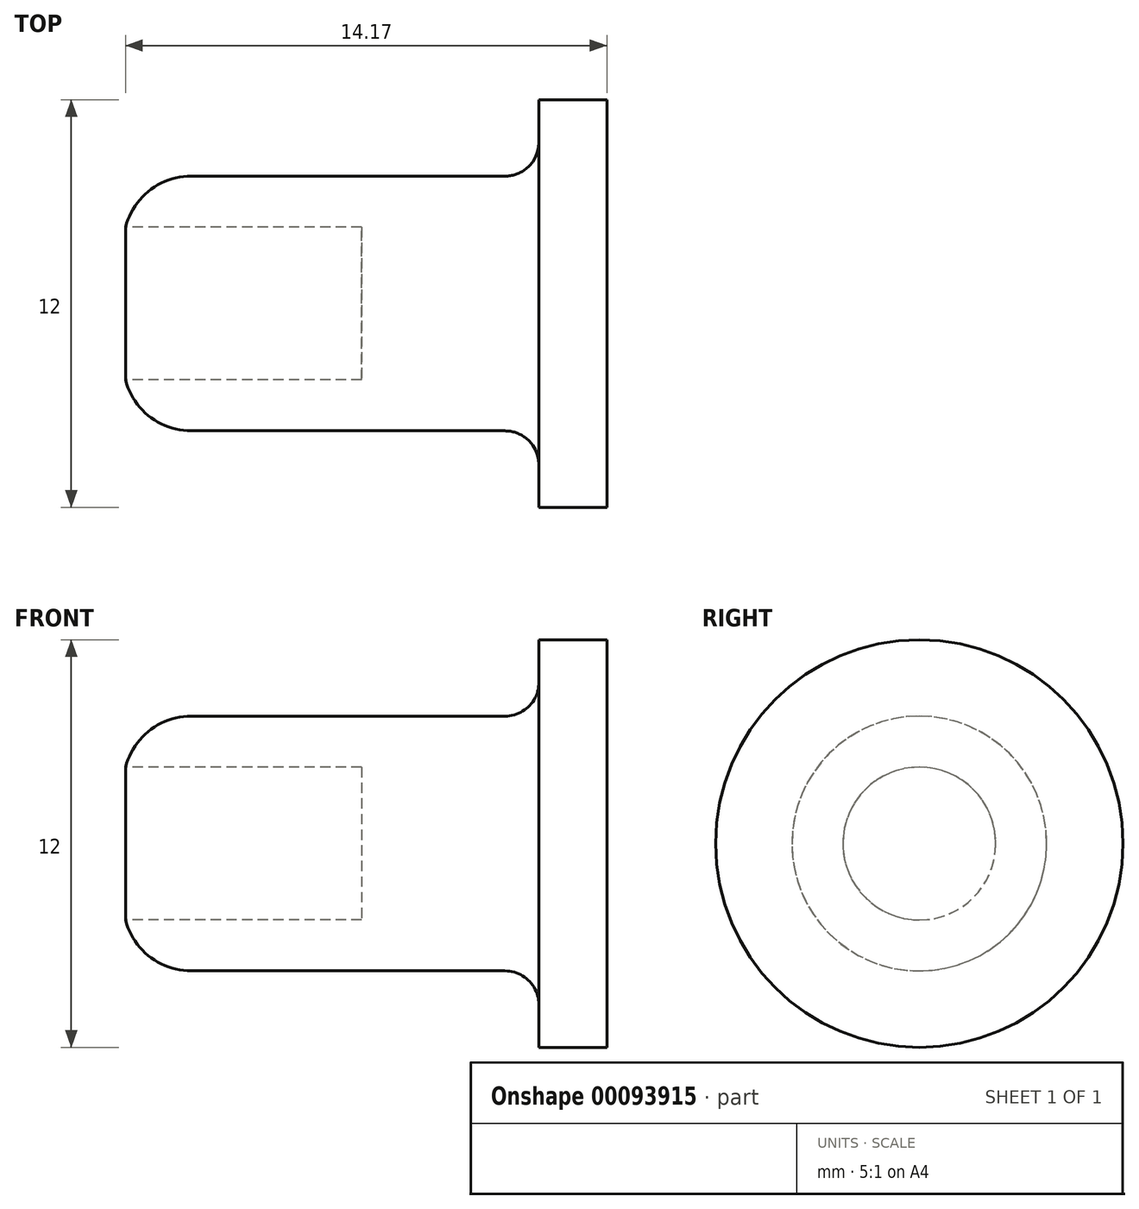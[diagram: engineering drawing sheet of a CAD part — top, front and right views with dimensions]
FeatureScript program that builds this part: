
annotation { "Feature Type Name" : "Feature", "Feature Type Description" : "" }
export const myFeature = defineFeature(function(context is Context, id is Id, definition is map)
    precondition{}
    {
        {
            var Q0;
            Q0=qCreatedBy(makeId("Front.planeOp"),FACE);
            var sketch = newSketch(context, id + "F0", { "sketchPlane" : qUnion([Q0])});
            skLineSegment(sketch, "E0", {"start": v(0, 0) * mm, "end": v(0, 6) * mm});
            skLineSegment(sketch, "E1", {"start": v(0, 6) * mm, "end": v(-2, 6) * mm});
            skLineSegment(sketch, "E2", {"start": v(-2, 6) * mm, "end": v(-2, 3.75) * mm});
            skLineSegment(sketch, "E3", {"start": v(-2, 3.75) * mm, "end": v(-11, 3.75) * mm});
            skLineSegment(sketch, "E4", {"start": v(-11, 3.75) * mm, "end": v(-12.24, 3.75) * mm});
            skLineSegment(sketch, "E5", {"start": v(-14.22, 2) * mm, "end": v(-14.22, 2) * mm});
            skLineSegment(sketch, "E6", {"start": v(-14.22, 2) * mm, "end": v(-14.22, 0) * mm});
            skLineSegment(sketch, "E7", {"start": v(-14.22, 0) * mm, "end": v(0, 0) * mm});
            skPoint(sketch, "E8.visualSharp", {"position": v(-14, 3.75) * mm});
            skArc(sketch, "E8.filletArc", {"start": v(-12.24, 3.75) * mm, "mid": v(-13.56, 3.25) * mm, "end": v(-14.22, 2) * mm});
            skSolve(sketch);
        }
        {
            var Q0;
            Q0=makeQuery(id+"F0.imprint","IMPRINT",FACE,{"disambiguationData":[TD([[makeQuery(id+"F0.imprint","IMPRINT",EDGE,{"derivedFrom":sQuery(id+"F0.wireOp",EDGE,"E0")}),1.0]])]});
            var Q1;
            Q1=sQuery(id+"F0.wireOp",EDGE,"E7");
            revolve(context, id + "F1", {"entities" : qUnion([Q0]), "axis" : qUnion([Q1]), "revolveType" : RevolveType.FULL});
        }
        {
            var Q0;
            Q0=makeQuery(id+"F1.opRevolve","SWEPT_EDGE",EDGE,{"disambiguationData":[OSD([sQuery(id+"F0.wireOp",EDGE,"E2"),sQuery(id+"F0.wireOp",EDGE,"E3")])]});
            fillet(context, id + "F2", {"entities" : qUnion([Q0]), "radius" : 1 * mm, "tangentPropagation" : true, "allowEdgeOverflow" : false});
        }
        {
            var Q0;
            Q0=makeQuery(id+"F1.opRevolve","SWEPT_FACE",FACE,{"disambiguationData":[OSD([sQuery(id+"F0.wireOp",EDGE,"E6")])]});
            var sketch = newSketch(context, id + "F3", { "sketchPlane" : qUnion([Q0])});
            skCircle(sketch, "E9", {"center": v(0, 0) * mm, "radius": 2.25 * mm});
            skSolve(sketch);
        }
        {
            var Q0;
            Q0 = qSketchRegion(id + "F3", true);
            extrude(context, id + "F4", {"entities" : qUnion([Q0]), "operationType" : NewBodyOperationType.REMOVE, "oppositeDirection" : true, "depth" : 7 * mm});
        }
    });
